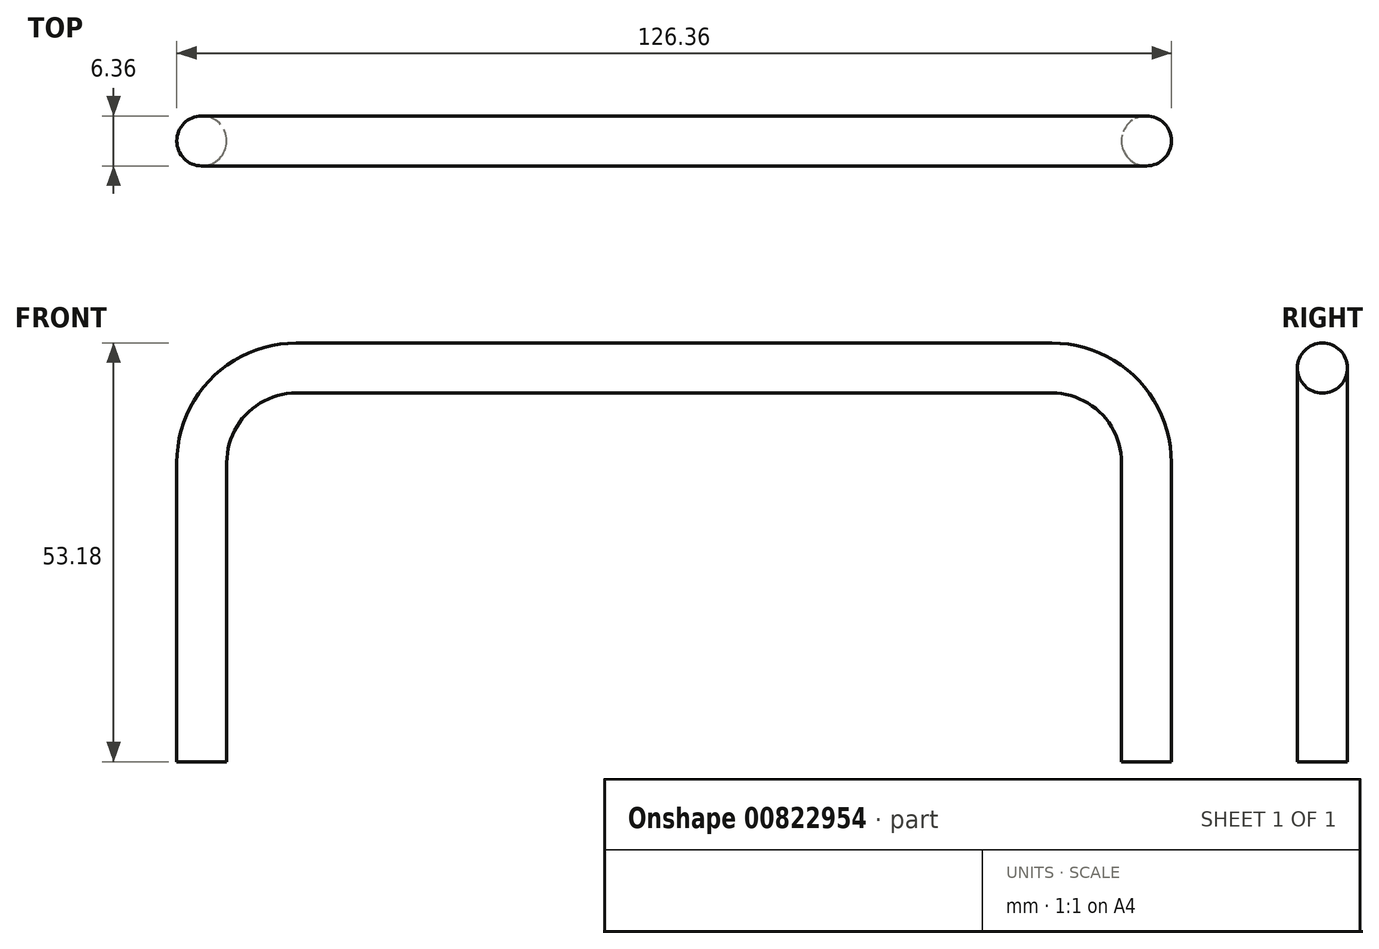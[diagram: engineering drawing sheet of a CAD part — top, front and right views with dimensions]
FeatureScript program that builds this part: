
annotation { "Feature Type Name" : "Feature", "Feature Type Description" : "" }
export const myFeature = defineFeature(function(context is Context, id is Id, definition is map)
    precondition{}
    {
        {
            var Q0;
            Q0=qCreatedBy(makeId("Front.planeOp"),FACE);
            var sketch = newSketch(context, id + "F0", { "sketchPlane" : qUnion([Q0])});
            skLineSegment(sketch, "E0", {"start": v(0, 0) * mm, "end": v(0, 38) * mm});
            skLineSegment(sketch, "E1", {"start": v(12, 50) * mm, "end": v(108, 50) * mm});
            skLineSegment(sketch, "E2", {"start": v(120, 38) * mm, "end": v(120, 0) * mm});
            skPoint(sketch, "E3.visualSharp", {"position": v(0, 50) * mm});
            skArc(sketch, "E3.filletArc", {"start": v(12, 50) * mm, "mid": v(3.51, 46.49) * mm, "end": v(0, 38) * mm});
            skPoint(sketch, "E4.visualSharp", {"position": v(120, 50) * mm});
            skArc(sketch, "E4.filletArc", {"start": v(120, 38) * mm, "mid": v(116.49, 46.49) * mm, "end": v(108, 50) * mm});
            skSolve(sketch);
        }
        {
            var Q0;
            Q0=qCreatedBy(makeId("Top.planeOp"),FACE);
            var sketch = newSketch(context, id + "F1", { "sketchPlane" : qUnion([Q0])});
            skCircle(sketch, "E5", {"center": v(0, 0) * mm, "radius": 3.18 * mm});
            skSolve(sketch);
        }
        {
            var Q0;
            Q0 = qSketchRegion(id + "F1", true);
            var Q1;
            Q1 = qConstructionFilter(qBodyType(qCreatedBy(id + "F0" ,EDGE), BodyType.WIRE), ConstructionObject.NO);
            sweep(context, id + "F2", {"profiles" : qUnion([Q0]), "path" : qUnion([Q1])});
        }
    });
